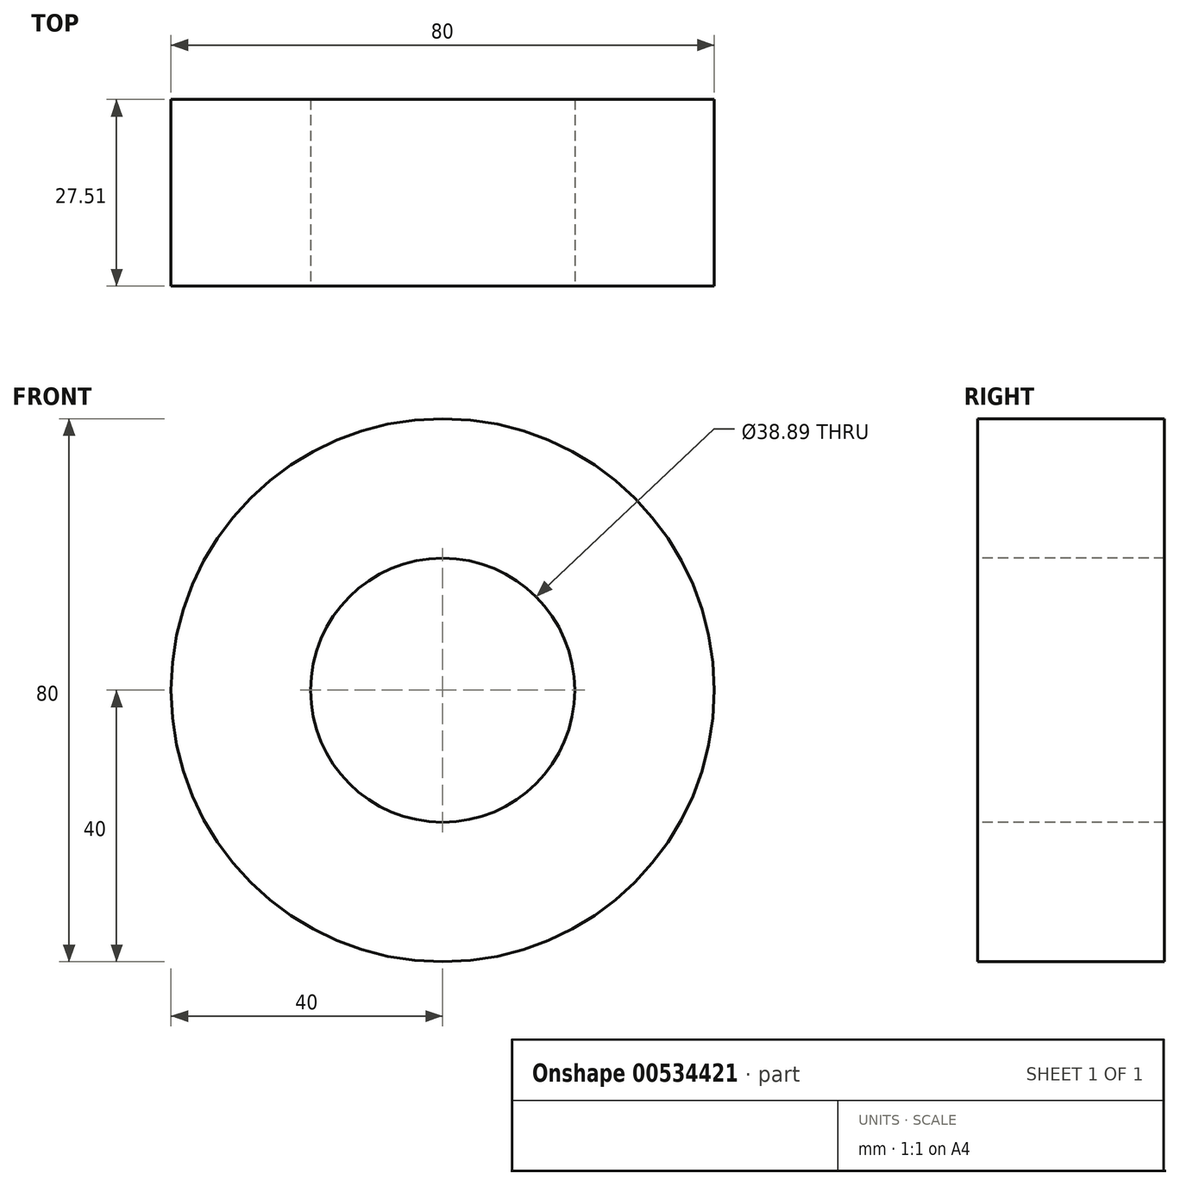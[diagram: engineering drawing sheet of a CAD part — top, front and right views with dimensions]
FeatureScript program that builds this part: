
annotation { "Feature Type Name" : "Feature", "Feature Type Description" : "" }
export const myFeature = defineFeature(function(context is Context, id is Id, definition is map)
    precondition{}
    {
        {
            var Q0;
            Q0=qCreatedBy(makeId("Front.planeOp"),FACE);
            var sketch = newSketch(context, id + "F0", { "sketchPlane" : qUnion([Q0])});
            skCircle(sketch, "E0", {"center": v(0, 0) * mm, "radius": 40 * mm});
            skCircle(sketch, "E1", {"center": v(0, 0) * mm, "radius": 19.45 * mm});
            skSolve(sketch);
        }
        {
            var Q0;
            Q0 = qSketchRegion(id + "F0", true);
            extrude(context, id + "F1", {"entities" : qUnion([Q0]), "oppositeDirection" : true, "depth" : 27.5 * mm, "offsetDistance" : 25.4 * mm});
        }
    });
